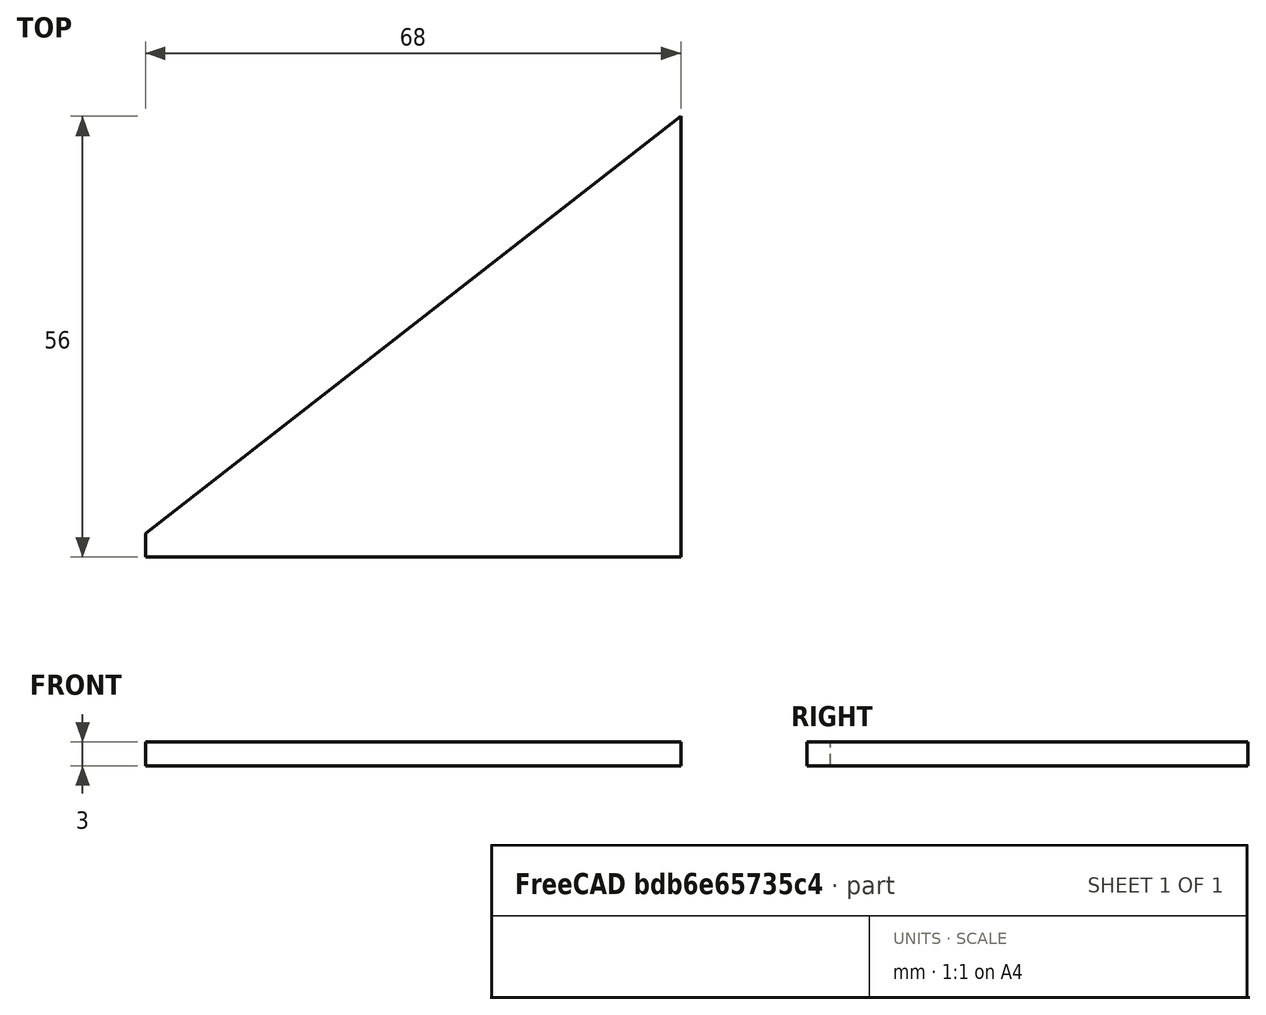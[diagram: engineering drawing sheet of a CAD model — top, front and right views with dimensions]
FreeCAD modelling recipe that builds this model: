
FCSTD DOCUMENT  (FreeCAD 0.19R24276 (Git))
Label: Nemo23_support_side_v3
License: All rights reserved
LicenseURL: http://en.wikipedia.org/wiki/All_rights_reserved
objects: Sketcher::SketchObject×1, PartDesign::Pad×1, PartDesign::Body×1
note: 4 computed .brp shape members not serialized (recipe doc carries the construction recipe); baked Part::Feature solids carry a one-line shape summary decoded from their .brp

FEATURE [Sketcher::SketchObject] Sketch
  FullyConstrained = true
  MapMode = 5
  Support = -> [XY_Plane]
  sketch-geometry (4):
    g0: LineSegment StartX=0 StartY=0 StartZ=0 EndX=-68 EndY=0 EndZ=0
    g1: LineSegment StartX=0 StartY=0 StartZ=0 EndX=0 EndY=56 EndZ=0
    g2: LineSegment StartX=-68 StartY=0 StartZ=0 EndX=-68 EndY=3 EndZ=0
    g3: LineSegment StartX=0 StartY=56 StartZ=0 EndX=-68 EndY=3 EndZ=0
  constraints (11):
    c: Coincident(g0,g-1)
    c: Horizontal(g0)
    c: Coincident(g1,g0)
    c: PointOnObject(g1,g-2)
    c: DistanceY(g1,g1) = 56
    c: DistanceX(g0,g0) = 68
    c: Coincident(g2,g0)
    c: Vertical(g2)
    c: DistanceY(g2,g2) = 3
    c: Coincident(g3,g1)
    c: Coincident(g3,g2)
FEATURE [PartDesign::Pad] Pad
  Direction = (1,1,1)
  Length = 3
  Length2 = 100
  Profile = -> Sketch
  Type = 0
FEATURE [PartDesign::Body] Body
  Group = -> [Sketch,Pad]
  Origin = -> Origin
  Tip = -> Pad
